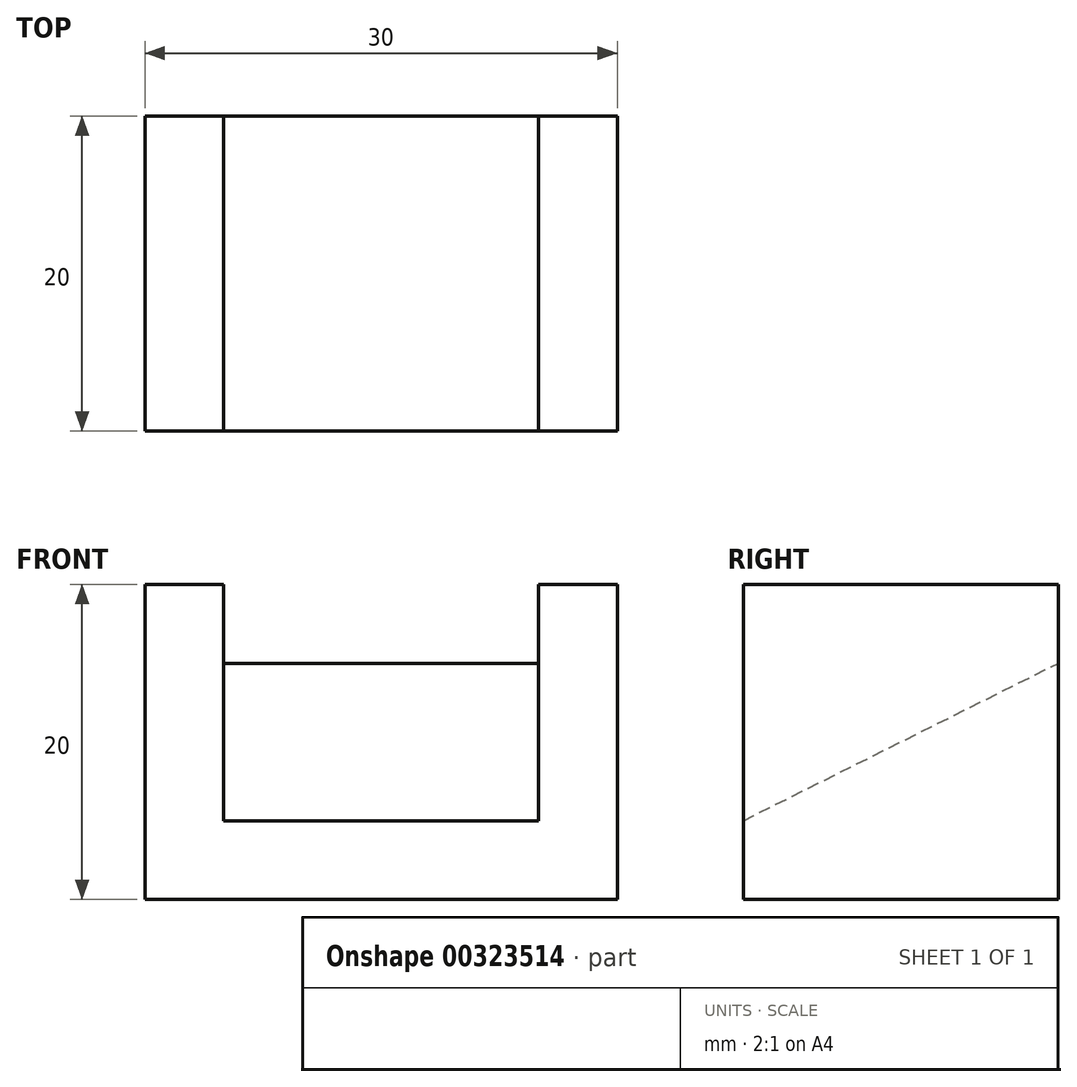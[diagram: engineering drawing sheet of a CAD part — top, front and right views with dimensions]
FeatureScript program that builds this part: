
annotation { "Feature Type Name" : "Feature", "Feature Type Description" : "" }
export const myFeature = defineFeature(function(context is Context, id is Id, definition is map)
    precondition{}
    {
        {
            var Q0;
            Q0=qCreatedBy(makeId("Front.planeOp"),FACE);
            var sketch = newSketch(context, id + "F0", { "sketchPlane" : qUnion([Q0])});
            skLineSegment(sketch, "E0", {"start": v(0, 0) * mm, "end": v(15, 0) * mm});
            skLineSegment(sketch, "E1", {"start": v(15, 0) * mm, "end": v(15, 20) * mm});
            skLineSegment(sketch, "E2", {"start": v(15, 20) * mm, "end": v(-15, 20) * mm});
            skLineSegment(sketch, "E3", {"start": v(-15, 20) * mm, "end": v(-15, 0) * mm});
            skLineSegment(sketch, "E4", {"start": v(-15, 0) * mm, "end": v(0, 0) * mm});
            skSolve(sketch);
        }
        {
            var Q0;
            Q0 = qSketchRegion(id + "F0", true);
            extrude(context, id + "F1", {"entities" : qUnion([Q0]), "depth" : 20 * mm});
        }
        {
            var Q0;
            Q0=qCreatedBy(makeId("Right.planeOp"),FACE);
            var sketch = newSketch(context, id + "F2", { "sketchPlane" : qUnion([Q0])});
            skLineSegment(sketch, "E5", {"start": v(0, 15) * mm, "end": v(0, 20) * mm});
            skLineSegment(sketch, "E6", {"start": v(0, 20) * mm, "end": v(-20, 20) * mm});
            skLineSegment(sketch, "E7", {"start": v(-20, 20) * mm, "end": v(-20, 5) * mm});
            skLineSegment(sketch, "E8", {"start": v(-20, 5) * mm, "end": v(0, 15) * mm});
            skSolve(sketch);
        }
        {
            var Q0;
            Q0 = qSketchRegion(id + "F2", true);
            extrude(context, id + "F3", {"entities" : qUnion([Q0]), "operationType" : NewBodyOperationType.REMOVE, "endBound" : BoundingType.SYMMETRIC, "oppositeDirection" : true, "depth" : 20 * mm});
        }
    });
